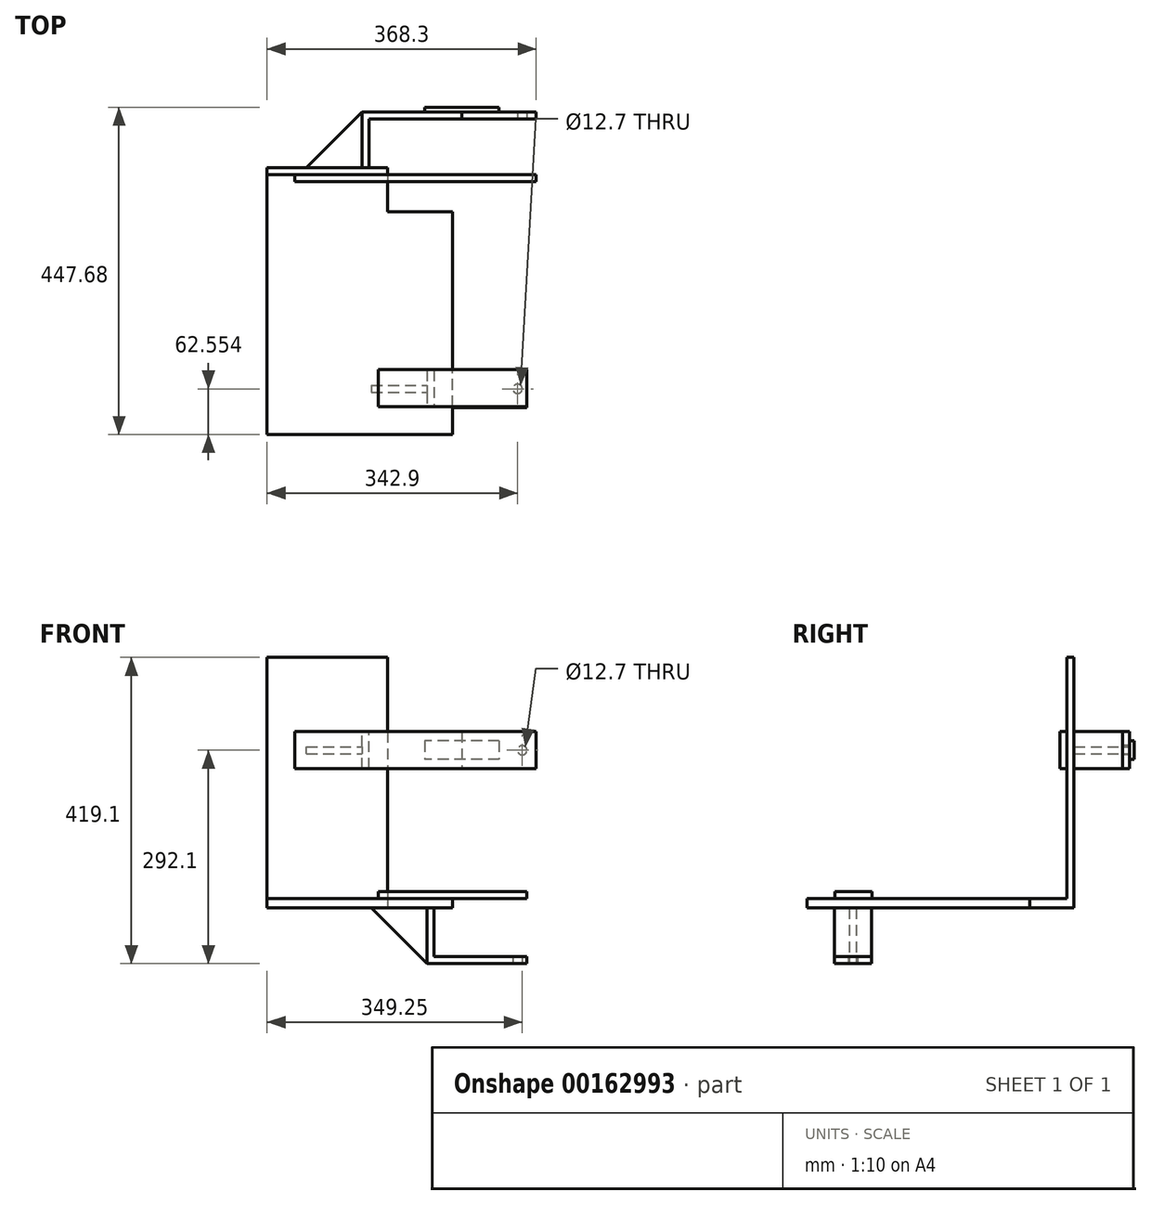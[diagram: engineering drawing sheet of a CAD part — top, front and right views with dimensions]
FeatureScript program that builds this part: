
annotation { "Feature Type Name" : "Feature", "Feature Type Description" : "" }
export const myFeature = defineFeature(function(context is Context, id is Id, definition is map)
    precondition{}
    {
        {
            var Q0;
            Q0=qCreatedBy(makeId("Top.planeOp"),FACE);
            var sketch = newSketch(context, id + "F0", { "sketchPlane" : qUnion([Q0])});
            skLineSegment(sketch, "E0.bottom", {"start": v(127, -177.8) * mm, "end": v(-127, -177.8) * mm});
            skLineSegment(sketch, "E0.top", {"start": v(38.1, 177.8) * mm, "end": v(-127, 177.8) * mm});
            skLineSegment(sketch, "E0.left", {"start": v(127, -177.8) * mm, "end": v(127, 127) * mm});
            skLineSegment(sketch, "E0.right", {"start": v(-127, -177.8) * mm, "end": v(-127, 177.8) * mm});
            skPoint(sketch, "E0.middle", {"position": v(0, 0) * mm});
            skLineSegment(sketch, "E1.top", {"start": v(127, 127) * mm, "end": v(38.1, 127) * mm});
            skLineSegment(sketch, "E1.right", {"start": v(38.1, 177.8) * mm, "end": v(38.1, 127) * mm});
            skPoint(sketch, "E2.orphan", {"position": v(127, 177.8) * mm});
            skSolve(sketch);
        }
        {
            var Q0;
            Q0 = qSketchRegion(id + "F0", true);
            extrude(context, id + "F1", {"entities" : qUnion([Q0]), "depth" : 12.7 * mm});
        }
        {
            var Q0;
            Q0=makeQuery(id+"F1.opExtrude","CAP_FACE",FACE,{"disambiguationData":[OSD([sQuery(id+"F0.wireOp",EDGE,"E0.bottom"),sQuery(id+"F0.wireOp",EDGE,"E0.top"),sQuery(id+"F0.wireOp",EDGE,"E0.left"),sQuery(id+"F0.wireOp",EDGE,"E0.right"),sQuery(id+"F0.wireOp",EDGE,"E1.top"),sQuery(id+"F0.wireOp",EDGE,"E1.right")])],"isStart":false});
            var sketch = newSketch(context, id + "F2", { "sketchPlane" : qUnion([Q0])});
            skLineSegment(sketch, "E3.bottom", {"start": v(25.4, -88.9) * mm, "end": v(228.6, -88.9) * mm});
            skLineSegment(sketch, "E3.top", {"start": v(25.4, -139.7) * mm, "end": v(228.6, -139.7) * mm});
            skLineSegment(sketch, "E3.left", {"start": v(25.4, -88.9) * mm, "end": v(25.4, -139.7) * mm});
            skLineSegment(sketch, "E3.right", {"start": v(228.6, -88.9) * mm, "end": v(228.6, -139.7) * mm});
            skSolve(sketch);
        }
        {
            var Q0;
            {var subQ0=sQuery(id+"F2.wireOp",EDGE,"E3.right");Q0=makeQuery(id+"F2.imprint","IMPRINT",FACE,{"disambiguationData":[TD([[makeQuery(id+"F2.imprint","IMPRINT",EDGE,{"derivedFrom":subQ0}),-1.0]])]});}
            var Q1;
            {var subQ0=sQuery(id+"F2.wireOp",EDGE,"E3.left");Q1=makeQuery(id+"F2.imprint","IMPRINT",FACE,{"disambiguationData":[TD([[makeQuery(id+"F2.imprint","IMPRINT",EDGE,{"derivedFrom":subQ0}),1.0]])]});}
            extrude(context, id + "F3", {"entities" : qUnion([Q0, Q1]), "operationType" : NewBodyOperationType.ADD, "depth" : 9.52 * mm});
        }
        {
            var Q0;
            Q0=makeQuery(id+"F1.opExtrude","SWEPT_FACE",FACE,{"disambiguationData":[OSD([sQuery(id+"F0.wireOp",EDGE,"E0.right")])]});
            var sketch = newSketch(context, id + "F4", { "sketchPlane" : qUnion([Q0])});
            skLineSegment(sketch, "E4.bottom", {"start": v(-177.8, 0) * mm, "end": v(-187.32, 0) * mm});
            skLineSegment(sketch, "E4.top", {"start": v(-177.8, 342.9) * mm, "end": v(-187.33, 342.9) * mm});
            skLineSegment(sketch, "E4.left", {"start": v(-177.8, 0) * mm, "end": v(-177.8, 342.9) * mm});
            skLineSegment(sketch, "E4.right", {"start": v(-187.32, 0) * mm, "end": v(-187.32, 342.9) * mm});
            skSolve(sketch);
        }
        {
            var Q0;
            Q0 = qSketchRegion(id + "F4", true);
            var Q1;
            Q1=makeQuery(id+"F1.opExtrude","SWEPT_FACE",FACE,{"disambiguationData":[OSD([sQuery(id+"F0.wireOp",EDGE,"E1.right")])]});
            extrude(context, id + "F5", {"entities" : qUnion([Q0]), "operationType" : NewBodyOperationType.ADD, "endBound" : BoundingType.UP_TO_SURFACE, "oppositeDirection" : true, "endBoundEntityFace" : qUnion([Q1]), "depth" : 25.4 * mm});
        }
        {
            var Q0;
            Q0=makeQuery(id+"F5.opExtrude","SWEPT_FACE",FACE,{"disambiguationData":[OSD([sQuery(id+"F4.wireOp",EDGE,"E4.left")])]});
            var sketch = newSketch(context, id + "F6", { "sketchPlane" : qUnion([Q0])});
            skLineSegment(sketch, "E5.bottom", {"start": v(-88.9, 241.3) * mm, "end": v(241.3, 241.3) * mm});
            skLineSegment(sketch, "E5.top", {"start": v(-88.9, 190.5) * mm, "end": v(241.3, 190.5) * mm});
            skLineSegment(sketch, "E5.left", {"start": v(-88.9, 241.3) * mm, "end": v(-88.9, 190.5) * mm});
            skLineSegment(sketch, "E5.right", {"start": v(241.3, 241.3) * mm, "end": v(241.3, 190.5) * mm});
            skSolve(sketch);
        }
        {
            var Q0;
            {var subQ0=sQuery(id+"F6.wireOp",EDGE,"E5.left");Q0=makeQuery(id+"F6.imprint","IMPRINT",FACE,{"disambiguationData":[TD([[makeQuery(id+"F6.imprint","IMPRINT",EDGE,{"derivedFrom":subQ0}),1.0]])]});}
            var Q1;
            {var subQ0=sQuery(id+"F6.wireOp",EDGE,"E5.right");Q1=makeQuery(id+"F6.imprint","IMPRINT",FACE,{"disambiguationData":[TD([[makeQuery(id+"F6.imprint","IMPRINT",EDGE,{"derivedFrom":subQ0}),-1.0]])]});}
            extrude(context, id + "F7", {"entities" : qUnion([Q0, Q1]), "operationType" : NewBodyOperationType.ADD, "depth" : 9.52 * mm});
        }
        {
            var Q0;
            Q0=makeQuery(id+"F5.boolean.opBoolean","MERGE",FACE,{"derivedFrom":[makeQuery(id+"F1.opExtrude","CAP_FACE",FACE,{"disambiguationData":[OSD([sQuery(id+"F0.wireOp",EDGE,"E0.bottom"),sQuery(id+"F0.wireOp",EDGE,"E0.top"),sQuery(id+"F0.wireOp",EDGE,"E0.left"),sQuery(id+"F0.wireOp",EDGE,"E0.right"),sQuery(id+"F0.wireOp",EDGE,"E1.top"),sQuery(id+"F0.wireOp",EDGE,"E1.right")])],"isStart":true}),makeQuery(id+"F5.opExtrude","SWEPT_FACE",FACE,{"disambiguationData":[OSD([sQuery(id+"F4.wireOp",EDGE,"E4.bottom")])]})]});
            var sketch = newSketch(context, id + "F8", { "sketchPlane" : qUnion([Q0])});
            skLineSegment(sketch, "E6.bottom", {"start": v(101.6, 89.85) * mm, "end": v(92.08, 89.85) * mm});
            skLineSegment(sketch, "E6.top", {"start": v(101.6, 140.65) * mm, "end": v(92.08, 140.65) * mm});
            skLineSegment(sketch, "E6.left", {"start": v(101.6, 89.85) * mm, "end": v(101.6, 140.65) * mm});
            skLineSegment(sketch, "E6.right", {"start": v(92.08, 89.85) * mm, "end": v(92.08, 140.65) * mm});
            skSolve(sketch);
        }
        {
            var Q0;
            Q0 = qSketchRegion(id + "F8", true);
            extrude(context, id + "F9", {"entities" : qUnion([Q0]), "operationType" : NewBodyOperationType.ADD, "depth" : 76.2 * mm});
        }
        {
            var Q0;
            Q0=makeQuery(id+"F9.opExtrude","SWEPT_FACE",FACE,{"disambiguationData":[OSD([sQuery(id+"F8.wireOp",EDGE,"E6.left")])]});
            var sketch = newSketch(context, id + "F10", { "sketchPlane" : qUnion([Q0])});
            skLineSegment(sketch, "E7.bottom", {"start": v(-89.85, -76.2) * mm, "end": v(-140.65, -76.2) * mm});
            skLineSegment(sketch, "E7.top", {"start": v(-89.85, -66.67) * mm, "end": v(-140.65, -66.67) * mm});
            skLineSegment(sketch, "E7.left", {"start": v(-89.85, -76.2) * mm, "end": v(-89.85, -66.67) * mm});
            skLineSegment(sketch, "E7.right", {"start": v(-140.65, -76.2) * mm, "end": v(-140.65, -66.67) * mm});
            skSolve(sketch);
        }
        {
            var Q0;
            Q0 = qSketchRegion(id + "F10", true);
            extrude(context, id + "F11", {"entities" : qUnion([Q0]), "operationType" : NewBodyOperationType.ADD, "depth" : 127 * mm});
        }
        {
            var Q0;
            Q0=makeQuery(id+"F9.opExtrude","SWEPT_FACE",FACE,{"disambiguationData":[OSD([sQuery(id+"F8.wireOp",EDGE,"E6.right")])]});
            var sketch = newSketch(context, id + "F12", { "sketchPlane" : qUnion([Q0])});
            skLineSegment(sketch, "E8.bottom", {"start": v(110.48, 0) * mm, "end": v(120, 0) * mm});
            skLineSegment(sketch, "E8.left", {"start": v(110.48, 0) * mm, "end": v(110.48, -76.2) * mm});
            skLineSegment(sketch, "E8.right", {"start": v(120, 0) * mm, "end": v(120, -76.2) * mm});
            skPoint(sketch, "E8.middle", {"position": v(115.25, -76.2) * mm});
            skLineSegment(sketch, "E9", {"start": v(110.48, -76.2) * mm, "end": v(120, -76.2) * mm});
            skPoint(sketch, "E8.top.end.orphan", {"position": v(120, -152.4) * mm});
            skPoint(sketch, "E8.top.start.orphan", {"position": v(110.48, -152.4) * mm});
            skSolve(sketch);
        }
        {
            var Q0;
            Q0 = qSketchRegion(id + "F12", true);
            extrude(context, id + "F13", {"entities" : qUnion([Q0]), "operationType" : NewBodyOperationType.ADD, "depth" : 76.2 * mm});
        }
        {
            var Q0;
            Q0=makeQuery(id+"F13.opExtrude","SWEPT_FACE",FACE,{"disambiguationData":[OSD([sQuery(id+"F12.wireOp",EDGE,"E8.right")])]});
            var sketch = newSketch(context, id + "F14", { "sketchPlane" : qUnion([Q0])});
            skLineSegment(sketch, "E10", {"start": v(15.88, 0) * mm, "end": v(15.88, -76.2) * mm});
            skLineSegment(sketch, "E11", {"start": v(15.88, -76.2) * mm, "end": v(92.08, -76.2) * mm});
            skLineSegment(sketch, "E12", {"start": v(92.08, -76.2) * mm, "end": v(15.88, 0) * mm});
            skSolve(sketch);
        }
        {
            var Q0;
            Q0 = qSketchRegion(id + "F14", true);
            extrude(context, id + "F15", {"entities" : qUnion([Q0]), "operationType" : NewBodyOperationType.REMOVE, "oppositeDirection" : true, "depth" : 25.4 * mm});
        }
        {
            var Q0;
            Q0=makeQuery(id+"F13.boolean.opBoolean","MERGE",FACE,{"derivedFrom":[makeQuery(id+"F11.boolean.opBoolean","MERGE",FACE,{"derivedFrom":[makeQuery(id+"F9.opExtrude","CAP_FACE",FACE,{"disambiguationData":[OSD([sQuery(id+"F8.wireOp",EDGE,"E6.bottom"),sQuery(id+"F8.wireOp",EDGE,"E6.top"),sQuery(id+"F8.wireOp",EDGE,"E6.left"),sQuery(id+"F8.wireOp",EDGE,"E6.right")])],"isStart":false}),makeQuery(id+"F11.opExtrude","SWEPT_FACE",FACE,{"disambiguationData":[OSD([sQuery(id+"F10.wireOp",EDGE,"E7.bottom")])]})]}),makeQuery(id+"F13.opExtrude","SWEPT_FACE",FACE,{"disambiguationData":[OSD([sQuery(id+"F12.wireOp",EDGE,"E9")])]})]});
            var sketch = newSketch(context, id + "F16", { "sketchPlane" : qUnion([Q0])});
            skCircle(sketch, "E13", {"center": v(215.9, 115.25) * mm, "radius": 6.35 * mm});
            skPoint(sketch, "E13.centerSnap0", {"position": v(228.6, 115.25) * mm});
            skSolve(sketch);
        }
        {
            var Q0;
            Q0 = qSketchRegion(id + "F16", true);
            extrude(context, id + "F17", {"entities" : qUnion([Q0]), "operationType" : NewBodyOperationType.REMOVE, "oppositeDirection" : true, "depth" : 25.4 * mm});
        }
        {
            var Q0;
            Q0=makeQuery(id+"F5.opExtrude","SWEPT_FACE",FACE,{"disambiguationData":[OSD([sQuery(id+"F4.wireOp",EDGE,"E4.right")])]});
            var sketch = newSketch(context, id + "F18", { "sketchPlane" : qUnion([Q0])});
            skLineSegment(sketch, "E14.bottom", {"start": v(-3.17, 190.5) * mm, "end": v(-12.7, 190.5) * mm});
            skLineSegment(sketch, "E14.top", {"start": v(-3.17, 241.3) * mm, "end": v(-12.7, 241.3) * mm});
            skLineSegment(sketch, "E14.left", {"start": v(-3.17, 190.5) * mm, "end": v(-3.17, 241.3) * mm});
            skLineSegment(sketch, "E14.right", {"start": v(-12.7, 190.5) * mm, "end": v(-12.7, 241.3) * mm});
            skSolve(sketch);
        }
        {
            var Q0;
            Q0 = qSketchRegion(id + "F18", true);
            extrude(context, id + "F19", {"entities" : qUnion([Q0]), "operationType" : NewBodyOperationType.ADD, "depth" : 76.2 * mm});
        }
        {
            var Q0;
            Q0=makeQuery(id+"F19.opExtrude","SWEPT_FACE",FACE,{"disambiguationData":[OSD([sQuery(id+"F18.wireOp",EDGE,"E14.right")])]});
            var sketch = newSketch(context, id + "F20", { "sketchPlane" : qUnion([Q0])});
            skLineSegment(sketch, "E15.bottom", {"start": v(263.53, 241.3) * mm, "end": v(254, 241.3) * mm});
            skLineSegment(sketch, "E15.top", {"start": v(263.53, 190.5) * mm, "end": v(254, 190.5) * mm});
            skLineSegment(sketch, "E15.left", {"start": v(263.53, 241.3) * mm, "end": v(263.53, 190.5) * mm});
            skLineSegment(sketch, "E15.right", {"start": v(254, 241.3) * mm, "end": v(254, 190.5) * mm});
            skSolve(sketch);
        }
        {
            var Q0;
            Q0=makeQuery(id+"F20.imprint","IMPRINT",FACE,{"disambiguationData":[TD([[makeQuery(id+"F20.imprint","IMPRINT",EDGE,{"derivedFrom":sQuery(id+"F20.wireOp",EDGE,"E15.bottom")}),1.0]])]});
            extrude(context, id + "F21", {"entities" : qUnion([Q0]), "operationType" : NewBodyOperationType.ADD, "depth" : 127 * mm});
        }
        {
            var Q0;
            Q0=makeQuery(id+"F21.opExtrude","CAP_FACE",FACE,{"disambiguationData":[OSD([sQuery(id+"F20.wireOp",EDGE,"E15.bottom"),sQuery(id+"F20.wireOp",EDGE,"E15.top"),sQuery(id+"F20.wireOp",EDGE,"E15.left"),sQuery(id+"F20.wireOp",EDGE,"E15.right")])],"isStart":false});
            extrude(context, id + "F22", {"entities" : qUnion([Q0]), "depth" : 101.6 * mm});
        }
        {
            var Q0;
            Q0=makeQuery(id+"F22.opExtrude","SWEPT_FACE",FACE,{"disambiguationData":[OSD([sQuery(id+"F20.wireOp",EDGE,"E15.left")])]});
            var sketch = newSketch(context, id + "F23", { "sketchPlane" : qUnion([Q0])});
            skLineSegment(sketch, "E16.bottom", {"start": v(-190.5, 228.6) * mm, "end": v(-88.9, 228.6) * mm});
            skLineSegment(sketch, "E16.top", {"start": v(-190.5, 203.2) * mm, "end": v(-88.9, 203.2) * mm});
            skLineSegment(sketch, "E16.left", {"start": v(-190.5, 228.6) * mm, "end": v(-190.5, 203.2) * mm});
            skLineSegment(sketch, "E16.right", {"start": v(-88.9, 228.6) * mm, "end": v(-88.9, 203.2) * mm});
            skPoint(sketch, "E16.middle", {"position": v(-139.7, 215.9) * mm});
            skSolve(sketch);
        }
        {
            var Q0;
            Q0 = qSketchRegion(id + "F23", true);
            extrude(context, id + "F24", {"entities" : qUnion([Q0]), "depth" : 6.35 * mm});
        }
        {
            var Q0;
            Q0=makeQuery(id+"F22.opExtrude","SWEPT_FACE",FACE,{"disambiguationData":[OSD([sQuery(id+"F20.wireOp",EDGE,"E15.right")])]});
            var sketch = newSketch(context, id + "F25", { "sketchPlane" : qUnion([Q0])});
            skCircle(sketch, "E17", {"center": v(222.25, 215.9) * mm, "radius": 6.35 * mm});
            skPoint(sketch, "E17.centerSnap0", {"position": v(241.3, 215.9) * mm});
            skSolve(sketch);
        }
        {
            var Q0;
            Q0 = qSketchRegion(id + "F25", true);
            extrude(context, id + "F26", {"entities" : qUnion([Q0]), "operationType" : NewBodyOperationType.REMOVE, "oppositeDirection" : true, "depth" : 25.4 * mm});
        }
        {
            var Q0;
            Q0=makeQuery(id+"F19.opExtrude","SWEPT_FACE",FACE,{"disambiguationData":[OSD([sQuery(id+"F18.wireOp",EDGE,"E14.left")])]});
            var sketch = newSketch(context, id + "F27", { "sketchPlane" : qUnion([Q0])});
            skLineSegment(sketch, "E18.bottom", {"start": v(-187.32, 211.14) * mm, "end": v(-263.53, 211.14) * mm});
            skLineSegment(sketch, "E18.top", {"start": v(-187.32, 220.66) * mm, "end": v(-263.53, 220.66) * mm});
            skLineSegment(sketch, "E18.left", {"start": v(-187.32, 211.14) * mm, "end": v(-187.32, 220.66) * mm});
            skPoint(sketch, "E18.middle", {"position": v(-263.53, 215.9) * mm});
            skLineSegment(sketch, "E19", {"start": v(-263.53, 211.14) * mm, "end": v(-263.53, 220.66) * mm});
            skPoint(sketch, "E18.right.end.orphan", {"position": v(-339.73, 220.66) * mm});
            skPoint(sketch, "E18.right.start.orphan", {"position": v(-339.73, 211.14) * mm});
            skSolve(sketch);
        }
        {
            var Q0;
            Q0 = qSketchRegion(id + "F27", true);
            extrude(context, id + "F28", {"entities" : qUnion([Q0]), "operationType" : NewBodyOperationType.ADD, "depth" : 76.2 * mm});
        }
        {
            var Q0;
            Q0=makeQuery(id+"F28.opExtrude","SWEPT_FACE",FACE,{"disambiguationData":[OSD([sQuery(id+"F27.wireOp",EDGE,"E18.bottom")])]});
            var sketch = newSketch(context, id + "F29", { "sketchPlane" : qUnion([Q0])});
            skLineSegment(sketch, "E20", {"start": v(3.17, -263.53) * mm, "end": v(-73.03, -187.32) * mm});
            skLineSegment(sketch, "E21", {"start": v(-73.03, -187.32) * mm, "end": v(-73.03, -263.53) * mm});
            skLineSegment(sketch, "E22", {"start": v(-73.03, -263.53) * mm, "end": v(3.17, -263.53) * mm});
            skSolve(sketch);
        }
        {
            var Q0;
            Q0 = qSketchRegion(id + "F29", true);
            extrude(context, id + "F30", {"entities" : qUnion([Q0]), "operationType" : NewBodyOperationType.REMOVE, "oppositeDirection" : true, "depth" : 25.4 * mm});
        }
    });
